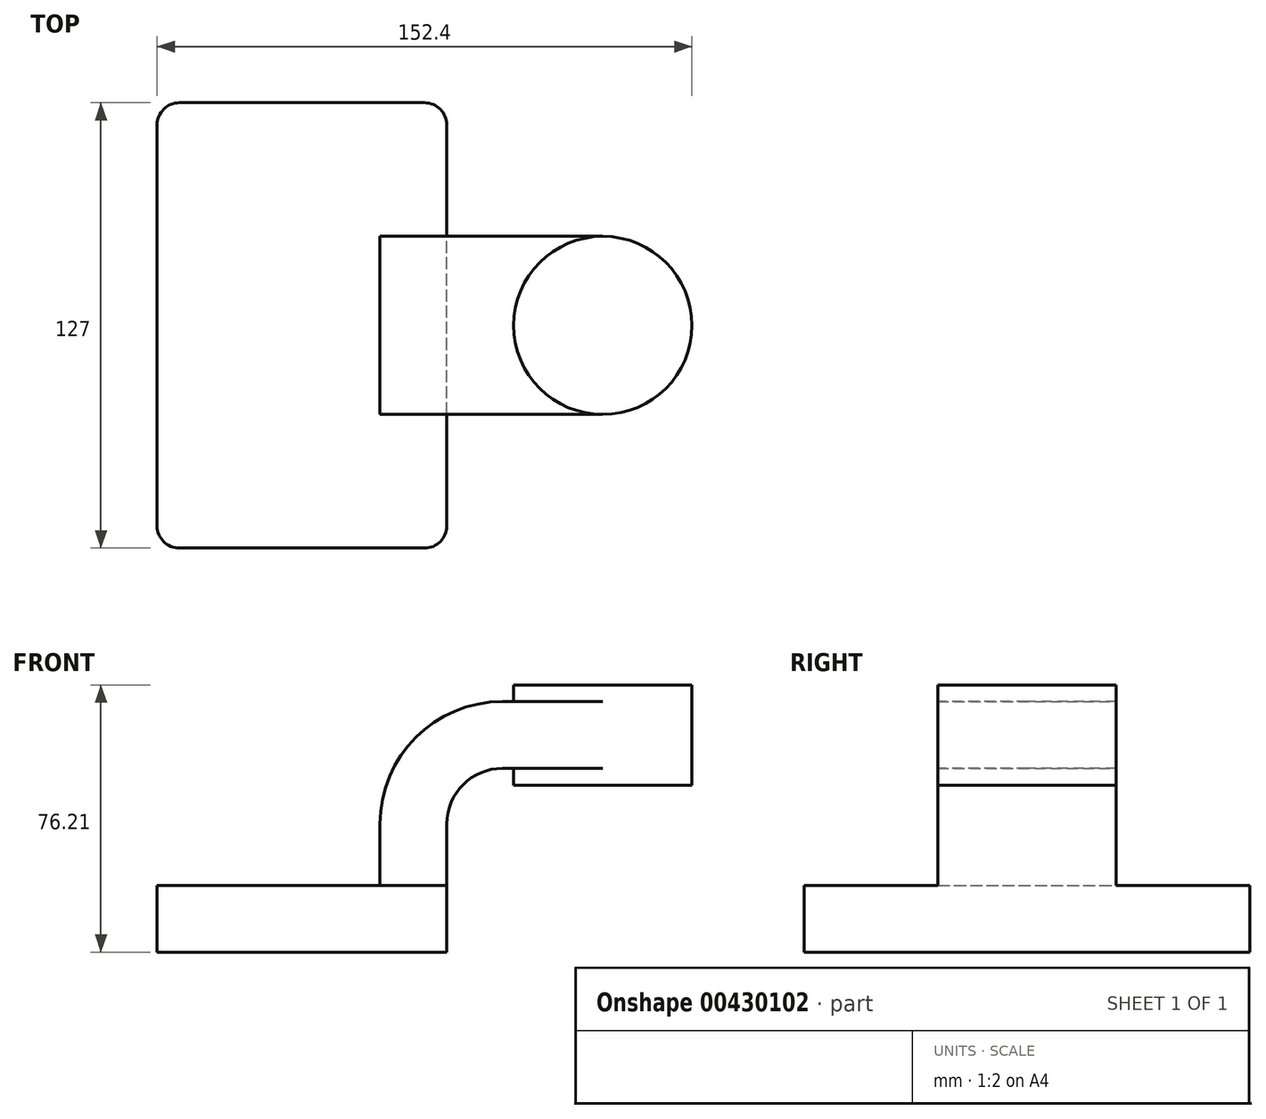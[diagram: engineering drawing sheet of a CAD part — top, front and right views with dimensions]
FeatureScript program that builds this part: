
annotation { "Feature Type Name" : "Feature", "Feature Type Description" : "" }
export const myFeature = defineFeature(function(context is Context, id is Id, definition is map)
    precondition{}
    {
        {
            var Q0;
            Q0=qCreatedBy(makeId("Front.planeOp"),FACE);
            var sketch = newSketch(context, id + "F0", { "sketchPlane" : qUnion([Q0])});
            skLineSegment(sketch, "E0.bottom", {"start": v(-41.28, 9.52) * mm, "end": v(41.28, 9.53) * mm});
            skLineSegment(sketch, "E0.top", {"start": v(-41.28, -9.53) * mm, "end": v(41.28, -9.52) * mm});
            skLineSegment(sketch, "E0.left", {"start": v(-41.28, 9.52) * mm, "end": v(-41.28, -9.53) * mm});
            skLineSegment(sketch, "E0.right", {"start": v(41.28, 9.53) * mm, "end": v(41.28, -9.52) * mm});
            skPoint(sketch, "E0.middle", {"position": v(0, 0) * mm});
            skLineSegment(sketch, "E1.bottom", {"start": v(60.33, 38.1) * mm, "end": v(111.13, 38.1) * mm});
            skLineSegment(sketch, "E1.top", {"start": v(60.32, 66.68) * mm, "end": v(111.13, 66.68) * mm});
            skLineSegment(sketch, "E1.left", {"start": v(60.33, 38.1) * mm, "end": v(60.32, 66.68) * mm});
            skLineSegment(sketch, "E1.right", {"start": v(111.13, 38.1) * mm, "end": v(111.13, 66.68) * mm});
            skPoint(sketch, "E1.middle", {"position": v(85.73, 52.39) * mm});
            skLineSegment(sketch, "E2", {"start": v(41.28, 9.53) * mm, "end": v(41.28, 27) * mm});
            skArc(sketch, "E3", {"start": v(41.27, 27) * mm, "mid": v(45.92, 38.23) * mm, "end": v(57.15, 42.88) * mm});
            skPoint(sketch, "E4.orphan", {"position": v(106.23, 42.88) * mm});
            skLineSegment(sketch, "E5", {"start": v(57.15, 42.88) * mm, "end": v(85.73, 42.88) * mm});
            skLineSegment(sketch, "E6.0", {"start": v(57.15, 61.93) * mm, "end": v(85.73, 61.93) * mm});
            skArc(sketch, "E6.1", {"start": v(22.23, 27) * mm, "mid": v(32.45, 51.7) * mm, "end": v(57.15, 61.93) * mm});
            skLineSegment(sketch, "E6.2", {"start": v(22.23, 9.53) * mm, "end": v(22.23, 27) * mm});
            skLineSegment(sketch, "E7", {"start": v(85.73, 38.1) * mm, "end": v(85.72, 66.68) * mm});
            skFitSpline(sketch, "E8", {"points": [v(-41.28, 9.52) * mm, v(57.15, 61.93) * mm], "startDerivative": vector(0, 85.73) * mm, "endDerivative": vector(171.45, 0) * mm});
            skSolve(sketch);
        }
        {
            var Q0;
            Q0=makeQuery(id+"F0.imprint","IMPRINT",FACE,{"disambiguationData":[TD([[makeQuery(id+"F0.imprint","IMPRINT",EDGE,{"derivedFrom":sQuery(id+"F0.wireOp",EDGE,"E0.top")}),1.0]])]});
            extrude(context, id + "F1", {"entities" : qUnion([Q0]), "endBound" : BoundingType.SYMMETRIC, "depth" : 127 * mm});
        }
        {
            var Q0;
            {var subQ1=sQuery(id+"F0.wireOp",EDGE,"E2");Q0=makeQuery(id+"F0.imprint","IMPRINT",FACE,{"disambiguationData":[TD([[makeQuery(id+"F0.imprint","IMPRINT",EDGE,{"derivedFrom":subQ1}),1.0]])]});}
            var Q1;
            {var subQ0=sQuery(id+"F0.wireOp",EDGE,"E5");var subQ1=sQuery(id+"F0.wireOp",EDGE,"E1.left");var subQ2=makeQuery(id+"F0.imprint","INTERSECT",VERTEX,{"derivedFrom":[subQ1,subQ0]});Q1=makeQuery(id+"F0.imprint","IMPRINT",FACE,{"disambiguationData":[TD([[makeQuery(id+"F0.imprint","IMPRINT",EDGE,{"disambiguationData":[TD([[subQ2,-1.0]])],"derivedFrom":subQ1}),-1.0]])]});}
            extrude(context, id + "F2", {"entities" : qUnion([Q0, Q1]), "operationType" : NewBodyOperationType.ADD, "endBound" : BoundingType.SYMMETRIC, "depth" : 50.8 * mm});
        }
        {
            var Q0;
            Q0=makeQuery(id+"F0.imprint","IMPRINT",FACE,{"disambiguationData":[TD([[makeQuery(id+"F0.imprint","IMPRINT",EDGE,{"derivedFrom":sQuery(id+"F0.wireOp",EDGE,"E6.1")}),1.0]])]});
            extrude(context, id + "F3", {"entities" : qUnion([Q0]), "operationType" : NewBodyOperationType.ADD, "endBound" : BoundingType.SYMMETRIC, "depth" : 15.88 * mm});
        }
        {
            var Q0;
            {var subQ0=sQuery(id+"F0.wireOp",EDGE,"E1.right");Q0=makeQuery(id+"F0.imprint","IMPRINT",FACE,{"disambiguationData":[TD([[makeQuery(id+"F0.imprint","IMPRINT",EDGE,{"derivedFrom":subQ0}),1.0]])]});}
            var Q1;
            Q1=sQuery(id+"F0.wireOp",EDGE,"E7");
            revolve(context, id + "F4", {"operationType" : NewBodyOperationType.ADD, "entities" : qUnion([Q0]), "axis" : qUnion([Q1]), "revolveType" : RevolveType.FULL});
        }
        {
            var Q0;
            Q0=makeQuery(id+"F1.opExtrude","CAP_EDGE",EDGE,{"disambiguationData":[OSD([sQuery(id+"F0.wireOp",EDGE,"E0.left")])],"isStart":false});
            var Q1;
            Q1=makeQuery(id+"F1.opExtrude","CAP_EDGE",EDGE,{"disambiguationData":[OSD([sQuery(id+"F0.wireOp",EDGE,"E0.right")])],"isStart":false});
            var Q2;
            Q2=makeQuery(id+"F1.opExtrude","CAP_EDGE",EDGE,{"disambiguationData":[OSD([sQuery(id+"F0.wireOp",EDGE,"E0.right")])],"isStart":true});
            var Q3;
            Q3=makeQuery(id+"F1.opExtrude","CAP_EDGE",EDGE,{"disambiguationData":[OSD([sQuery(id+"F0.wireOp",EDGE,"E0.left")])],"isStart":true});
            fillet(context, id + "F5", {"entities" : qUnion([Q0, Q1, Q2, Q3]), "radius" : 6.35 * mm, "tangentPropagation" : true, "allowEdgeOverflow" : false});
        }
    });
